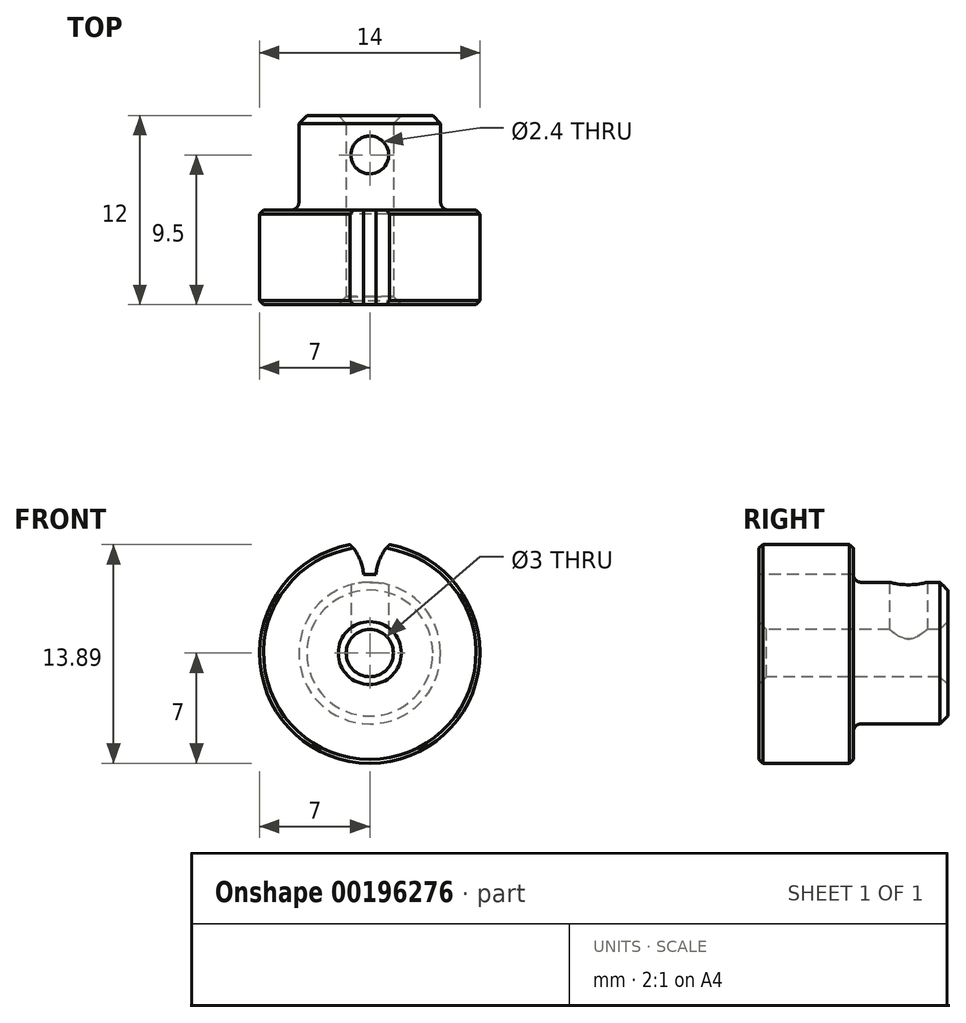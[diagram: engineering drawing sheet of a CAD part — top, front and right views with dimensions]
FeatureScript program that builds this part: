
annotation { "Feature Type Name" : "Feature", "Feature Type Description" : "" }
export const myFeature = defineFeature(function(context is Context, id is Id, definition is map)
    precondition{}
    {
        {
            var Q0;
            Q0=qCreatedBy(makeId("Right.planeOp"),FACE);
            var sketch = newSketch(context, id + "F0", { "sketchPlane" : qUnion([Q0])});
            skLineSegment(sketch, "E0", {"start": v(0, 0) * mm, "end": v(12, 0) * mm, "construction": true});
            skLineSegment(sketch, "E1", {"start": v(0, 1.5) * mm, "end": v(0, 7) * mm});
            skLineSegment(sketch, "E2", {"start": v(0, 7) * mm, "end": v(6, 7) * mm});
            skLineSegment(sketch, "E3", {"start": v(6, 7) * mm, "end": v(6, 4.5) * mm});
            skLineSegment(sketch, "E4", {"start": v(6, 4.5) * mm, "end": v(12, 4.5) * mm});
            skLineSegment(sketch, "E5", {"start": v(12, 4.5) * mm, "end": v(12, 1.5) * mm});
            skLineSegment(sketch, "E6", {"start": v(0, 1.5) * mm, "end": v(12, 1.5) * mm});
            skSolve(sketch);
        }
        {
            var Q0;
            Q0 = qSketchRegion(id + "F0", true);
            var Q1;
            Q1=sQuery(id+"F0.wireOp",EDGE,"E0");
            revolve(context, id + "F1", {"entities" : qUnion([Q0]), "axis" : qUnion([Q1]), "revolveType" : RevolveType.FULL});
        }
        {
            var Q0;
            Q0=makeQuery(id+"F1.opRevolve","SWEPT_FACE",FACE,{"disambiguationData":[OSD([sQuery(id+"F0.wireOp",EDGE,"E1")])]});
            var sketch = newSketch(context, id + "F2", { "sketchPlane" : qUnion([Q0])});
            skLineSegment(sketch, "E7", {"start": v(0, 0) * mm, "end": v(0, 7) * mm, "construction": true});
            skArc(sketch, "E8.0", {"start": v(0, 7) * mm, "mid": v(-0.63, 6.97) * mm, "end": v(-1.25, 6.89) * mm});
            skArc(sketch, "E9", {"start": v(0, 5) * mm, "mid": v(-0.2, 5) * mm, "end": v(-0.4, 4.98) * mm});
            skArc(sketch, "E10", {"start": v(-0.4, 4.98) * mm, "mid": v(-0.65, 6.01) * mm, "end": v(-1.25, 6.89) * mm});
            skArc(sketch, "E11.MirrorCS", {"start": v(0, 7) * mm, "mid": v(0.63, 6.97) * mm, "end": v(1.25, 6.89) * mm});
            skArc(sketch, "E12.MirrorCS", {"start": v(0, 5) * mm, "mid": v(0.2, 5) * mm, "end": v(0.4, 4.98) * mm});
            skArc(sketch, "E13.MirrorCS", {"start": v(0.4, 4.98) * mm, "mid": v(0.65, 6.01) * mm, "end": v(1.25, 6.89) * mm});
            skSolve(sketch);
        }
        {
            var Q0;
            Q0 = qSketchRegion(id + "F2", true);
            extrude(context, id + "F3", {"entities" : qUnion([Q0]), "operationType" : NewBodyOperationType.REMOVE, "endBound" : BoundingType.THROUGH_ALL, "oppositeDirection" : true, "depth" : 25 * mm});
        }
        {
            var Q0;
            Q0=makeQuery(id+"F1.opRevolve","SWEPT_EDGE",EDGE,{"disambiguationData":[OSD([sQuery(id+"F0.wireOp",EDGE,"E1"),sQuery(id+"F0.wireOp",EDGE,"E2")])]});
            var Q1;
            Q1=makeQuery(id+"F1.opRevolve","SWEPT_EDGE",EDGE,{"disambiguationData":[OSD([sQuery(id+"F0.wireOp",EDGE,"E2"),sQuery(id+"F0.wireOp",EDGE,"E3")])]});
            chamfer(context, id + "F4", {"entities" : qUnion([Q0, Q1]), "width" : .25 * mm, "tangentPropagation" : true});
        }
        {
            var Q0;
            Q0=makeQuery(id+"F1.opRevolve","SWEPT_EDGE",EDGE,{"disambiguationData":[OSD([sQuery(id+"F0.wireOp",EDGE,"E1"),sQuery(id+"F0.wireOp",EDGE,"E6")])]});
            var Q1;
            Q1=makeQuery(id+"F1.opRevolve","SWEPT_EDGE",EDGE,{"disambiguationData":[OSD([sQuery(id+"F0.wireOp",EDGE,"E5"),sQuery(id+"F0.wireOp",EDGE,"E6")])]});
            var Q2;
            Q2=makeQuery(id+"F1.opRevolve","SWEPT_EDGE",EDGE,{"disambiguationData":[OSD([sQuery(id+"F0.wireOp",EDGE,"E4"),sQuery(id+"F0.wireOp",EDGE,"E5")])]});
            chamfer(context, id + "F5", {"entities" : qUnion([Q0, Q1, Q2]), "width" : 0.5 * mm, "tangentPropagation" : true});
        }
        {
            var Q0;
            Q0=makeQuery(id+"F1.opRevolve","SWEPT_EDGE",EDGE,{"disambiguationData":[OSD([sQuery(id+"F0.wireOp",EDGE,"E3"),sQuery(id+"F0.wireOp",EDGE,"E4")])]});
            fillet(context, id + "F6", {"entities" : qUnion([Q0]), "radius" : .5 * mm, "tangentPropagation" : true, "allowEdgeOverflow" : false});
        }
        {
            var Q0;
            Q0=qCreatedBy(makeId("Top.planeOp"),FACE);
            var sketch = newSketch(context, id + "F7", { "sketchPlane" : qUnion([Q0])});
            skPoint(sketch, "E14", {"position": v(0, 9.5) * mm});
            skSolve(sketch);
        }
        {
            var Q0;
            Q0=sQuery(id+"F7.wireOp",VERTEX,"E14");
            var Q1;
            Q1=makeQuery(id+"F1.opRevolve","SWEPT_BODY",BODY,{"disambiguationData":[OSD([sQuery(id+"F0.wireOp",EDGE,"E1"),sQuery(id+"F0.wireOp",EDGE,"E2"),sQuery(id+"F0.wireOp",EDGE,"E3"),sQuery(id+"F0.wireOp",EDGE,"E4"),sQuery(id+"F0.wireOp",EDGE,"E5"),sQuery(id+"F0.wireOp",EDGE,"E6")])]});
            hole(context, id + "F8", {"style" : HoleStyle.SIMPLE, "endStyle" : HoleEndStyle.THROUGH, "oppositeDirection" : true, "standardTappedOrClearance" : lookupTablePath({ "standard" : "ISO", "engagement" : "75%", "pitch" : "0.6 mm", "size" : "M3", "type" : "Tapped" }), "standardBlindInLast" : lookupTablePath({ "standard" : "ISO", "engagement" : "75%", "pitch" : "0.6 mm", "size" : "M3", "type" : "Tapped" }), "holeDiameter" : 2.4 * mm, "locations" : qUnion([Q0]), "scope" : qUnion([Q1]), "isTappedThrough" : true, "showTappedDepth" : true});
        }
    });
